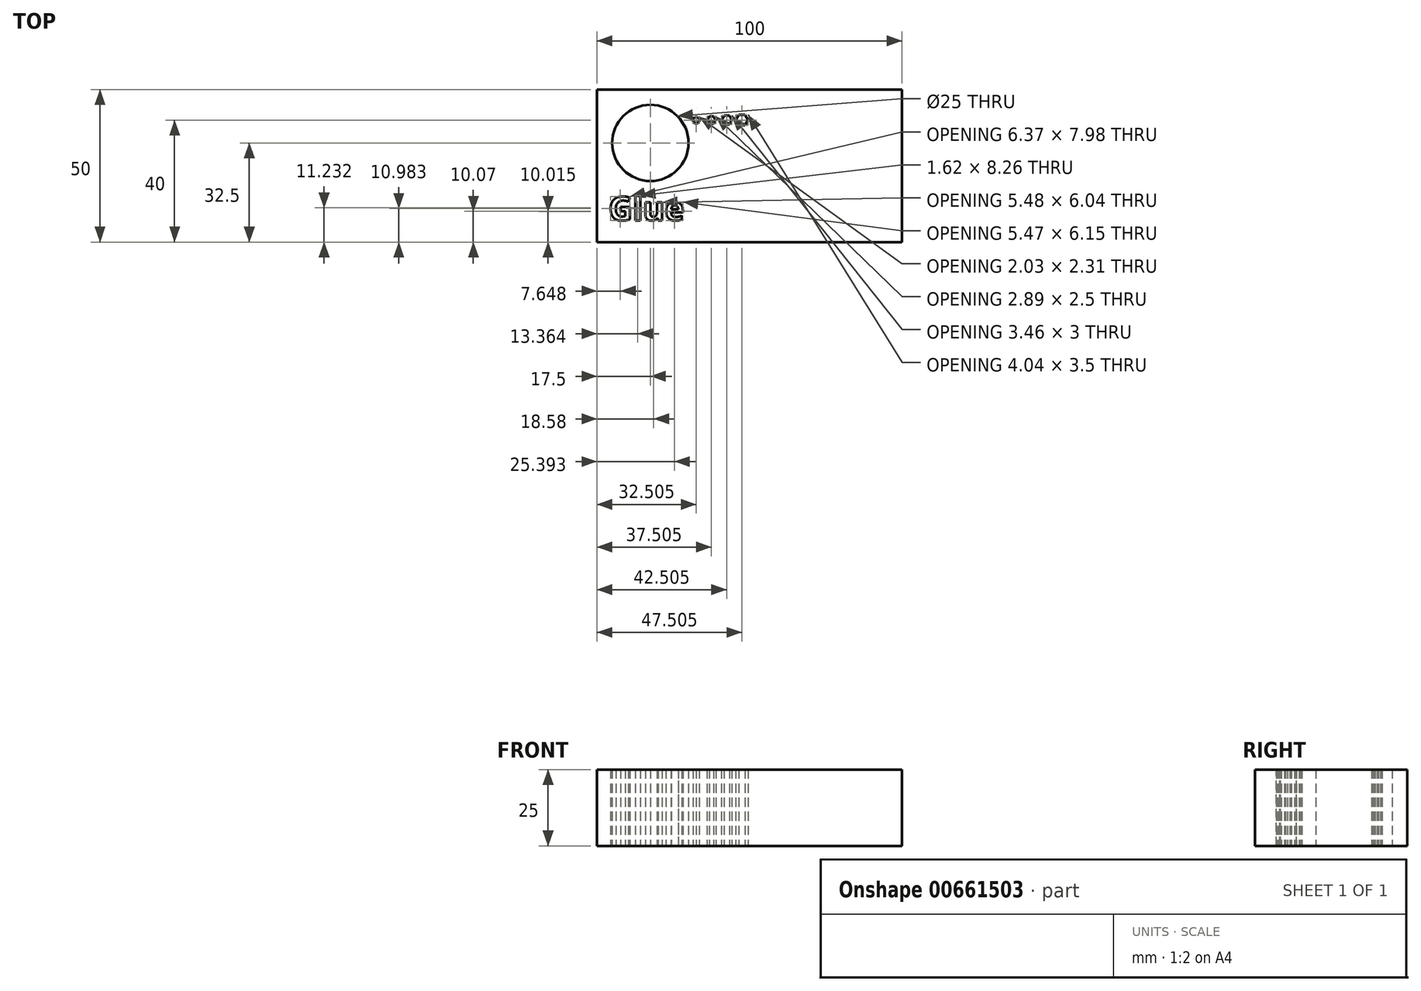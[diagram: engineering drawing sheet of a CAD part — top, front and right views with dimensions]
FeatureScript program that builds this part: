
annotation { "Feature Type Name" : "Feature", "Feature Type Description" : "" }
export const myFeature = defineFeature(function(context is Context, id is Id, definition is map)
    precondition{}
    {
        {
            var Q0;
            Q0=qCreatedBy(makeId("Top.planeOp"),FACE);
            var sketch = newSketch(context, id + "F0", { "sketchPlane" : qUnion([Q0])});
            skLineSegment(sketch, "E0.bottom", {"start": v(-50, 25) * mm, "end": v(50, 25) * mm});
            skLineSegment(sketch, "E0.top", {"start": v(-50, -25) * mm, "end": v(50, -25) * mm});
            skLineSegment(sketch, "E0.left", {"start": v(-50, 25) * mm, "end": v(-50, -25) * mm});
            skLineSegment(sketch, "E0.right", {"start": v(50, 25) * mm, "end": v(50, -25) * mm});
            skCircle(sketch, "E1", {"center": v(-32.5, 7.5) * mm, "radius": 12.5 * mm});
            skText(sketch, "E2", { "text": "Glue", "fontName": "OpenSans-Bold.ttf"});
            skLineSegment(sketch, "E3", {"start": v(-50, 15) * mm, "end": v(50, 15) * mm, "construction": true});
            skCircle(sketch, "E4.cCircle", {"center": v(-17.5, 15) * mm, "radius": 1 * mm, "construction": true});
            skLineSegment(sketch, "E4.0", {"start": v(-16.48, 14.45) * mm, "end": v(-17.47, 13.85) * mm});
            skLineSegment(sketch, "E4.1", {"start": v(-17.47, 13.85) * mm, "end": v(-18.48, 14.4) * mm});
            skLineSegment(sketch, "E4.2", {"start": v(-18.48, 14.4) * mm, "end": v(-18.5, 15.55) * mm});
            skLineSegment(sketch, "E4.3", {"start": v(-18.5, 15.55) * mm, "end": v(-17.52, 16.15) * mm});
            skLineSegment(sketch, "E4.4", {"start": v(-17.52, 16.15) * mm, "end": v(-16.5, 15.6) * mm});
            skLineSegment(sketch, "E4.5", {"start": v(-16.5, 15.6) * mm, "end": v(-16.48, 14.45) * mm});
            skPoint(sketch, "E4.0.midPoint", {"position": v(-16.98, 14.15) * mm});
            skCircle(sketch, "E5.cCircle", {"center": v(-12.5, 15) * mm, "radius": 1.25 * mm, "construction": true});
            skLineSegment(sketch, "E5.0", {"start": v(-13.22, 16.25) * mm, "end": v(-11.77, 16.25) * mm});
            skLineSegment(sketch, "E5.1", {"start": v(-11.77, 16.25) * mm, "end": v(-11.05, 15) * mm});
            skLineSegment(sketch, "E5.2", {"start": v(-11.05, 15) * mm, "end": v(-11.77, 13.75) * mm});
            skLineSegment(sketch, "E5.3", {"start": v(-11.77, 13.75) * mm, "end": v(-13.22, 13.75) * mm});
            skLineSegment(sketch, "E5.4", {"start": v(-13.22, 13.75) * mm, "end": v(-13.94, 15) * mm});
            skLineSegment(sketch, "E5.5", {"start": v(-13.94, 15) * mm, "end": v(-13.22, 16.25) * mm});
            skPoint(sketch, "E5.0.midPoint", {"position": v(-12.5, 16.25) * mm});
            skCircle(sketch, "E6.cCircle", {"center": v(-7.5, 15) * mm, "radius": 1.5 * mm, "construction": true});
            skLineSegment(sketch, "E6.0", {"start": v(-5.76, 15) * mm, "end": v(-6.63, 13.5) * mm});
            skLineSegment(sketch, "E6.1", {"start": v(-6.63, 13.5) * mm, "end": v(-8.36, 13.5) * mm});
            skLineSegment(sketch, "E6.2", {"start": v(-8.36, 13.5) * mm, "end": v(-9.23, 15) * mm});
            skLineSegment(sketch, "E6.3", {"start": v(-9.23, 15) * mm, "end": v(-8.36, 16.5) * mm});
            skLineSegment(sketch, "E6.4", {"start": v(-8.36, 16.5) * mm, "end": v(-6.63, 16.5) * mm});
            skLineSegment(sketch, "E6.5", {"start": v(-6.63, 16.5) * mm, "end": v(-5.76, 15) * mm});
            skPoint(sketch, "E6.0.midPoint", {"position": v(-6.2, 14.25) * mm});
            skCircle(sketch, "E7.cCircle", {"center": v(-2.5, 15) * mm, "radius": 1.75 * mm, "construction": true});
            skLineSegment(sketch, "E7.0", {"start": v(-0.47, 15) * mm, "end": v(-1.48, 13.25) * mm});
            skLineSegment(sketch, "E7.1", {"start": v(-1.48, 13.25) * mm, "end": v(-3.5, 13.25) * mm});
            skLineSegment(sketch, "E7.2", {"start": v(-3.5, 13.25) * mm, "end": v(-4.52, 15) * mm});
            skLineSegment(sketch, "E7.3", {"start": v(-4.52, 15) * mm, "end": v(-3.5, 16.75) * mm});
            skLineSegment(sketch, "E7.4", {"start": v(-3.5, 16.75) * mm, "end": v(-1.48, 16.75) * mm});
            skLineSegment(sketch, "E7.5", {"start": v(-1.48, 16.75) * mm, "end": v(-0.47, 15) * mm});
            skPoint(sketch, "E7.0.midPoint", {"position": v(-0.98, 14.13) * mm});
            const initialGuessF0  = {"E2": [-0.04617, -0.0179, 1, 0, 0.00783]};
            skSetInitialGuess(sketch, initialGuessF0);
            skSolve(sketch);
        }
        {
            var Q0;
            Q0=makeQuery(id+"F0.imprint","IMPRINT",FACE,{"disambiguationData":[TD([[makeQuery(id+"F0.imprint","IMPRINT",EDGE,{"derivedFrom":sQuery(id+"F0.wireOp",EDGE,"E0.bottom")}),-1.0]])]});
            var Q1;
            Q1=makeQuery(id+"F0.imprint","IMPRINT",FACE,{"disambiguationData":[TD([[makeQuery(id+"F0.imprint","IMPRINT",EDGE,{"derivedFrom":sQuery(id+"F0.wireOp",EDGE,"E2.sketch_text.stroke-40")}),1.0]])]});
            extrude(context, id + "F1", {"entities" : qUnion([Q0, Q1]), "depth" : 25 * mm, "offsetDistance" : 25 * mm});
        }
    });
